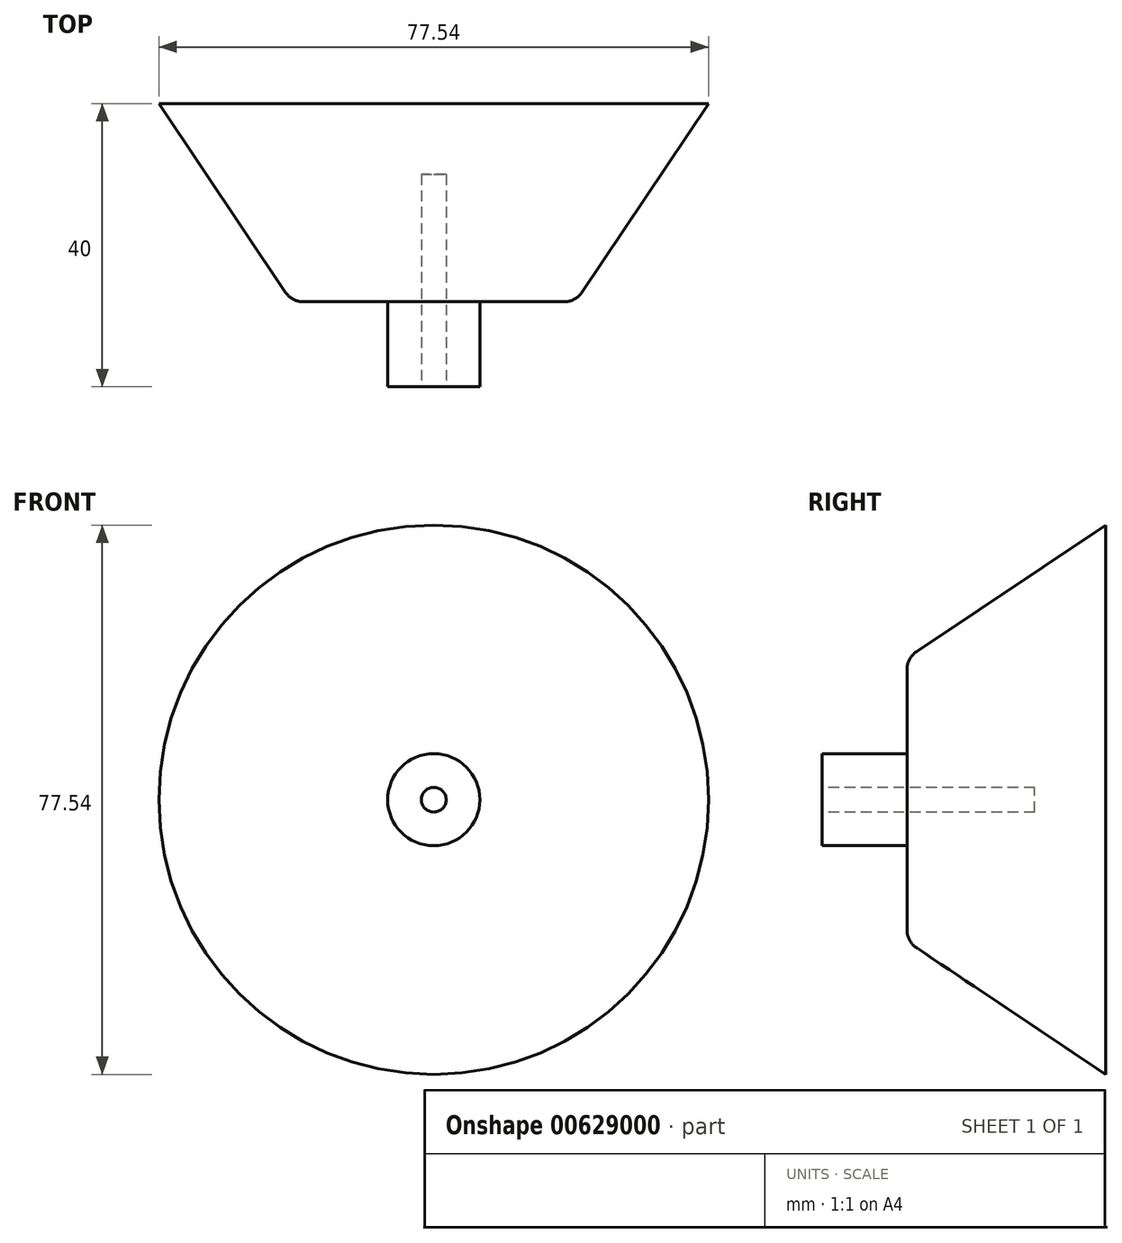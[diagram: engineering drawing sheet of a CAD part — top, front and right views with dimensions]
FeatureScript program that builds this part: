
annotation { "Feature Type Name" : "Feature", "Feature Type Description" : "" }
export const myFeature = defineFeature(function(context is Context, id is Id, definition is map)
    precondition{}
    {
        {
            var Q0;
            Q0=qCreatedBy(makeId("Front.planeOp"),FACE);
            var sketch = newSketch(context, id + "F0", { "sketchPlane" : qUnion([Q0])});
            skCircle(sketch, "E0", {"center": v(0, 0) * mm, "radius": 1.75 * mm});
            skCircle(sketch, "E1", {"center": v(0, 0) * mm, "radius": 6.5 * mm});
            skSolve(sketch);
        }
        {
            var Q0;
            Q0=qCreatedBy(makeId("Right.planeOp"),FACE);
            var sketch = newSketch(context, id + "F1", { "sketchPlane" : qUnion([Q0])});
            skLineSegment(sketch, "E2", {"start": v(0, 9.44) * mm, "end": v(0, -12.72) * mm, "construction": true});
            skLineSegment(sketch, "E3", {"start": v(12, 9.44) * mm, "end": v(12, -12.24) * mm, "construction": true});
            skLineSegment(sketch, "E4", {"start": v(40, 9.44) * mm, "end": v(40, -12.24) * mm, "construction": true});
            skLineSegment(sketch, "E5", {"start": v(12, 0) * mm, "end": v(12, 20) * mm});
            skLineSegment(sketch, "E6", {"start": v(40, 0) * mm, "end": v(12, 0) * mm});
            skLineSegment(sketch, "E7", {"start": v(5.3, 0) * mm, "end": v(66.6, 0) * mm, "construction": true});
            skLineSegment(sketch, "E8", {"start": v(12, 20) * mm, "end": v(40, 38.77) * mm});
            skLineSegment(sketch, "E9", {"start": v(40, 38.77) * mm, "end": v(40, 0) * mm});
            skSolve(sketch);
        }
        {
            var Q0;
            Q0=makeQuery(id+"F1.imprint","IMPRINT",FACE,{"disambiguationData":[TD([[makeQuery(id+"F1.imprint","IMPRINT",EDGE,{"derivedFrom":sQuery(id+"F1.wireOp",EDGE,"E5")}),-1.0]])]});
            var Q1;
            Q1=sQuery(id+"F1.wireOp",EDGE,"E7");
            revolve(context, id + "F2", {"entities" : qUnion([Q0]), "axis" : qUnion([Q1]), "revolveType" : RevolveType.FULL});
        }
        {
            var Q0;
            Q0=makeQuery(id+"F0.imprint","IMPRINT",FACE,{"disambiguationData":[TD([[makeQuery(id+"F0.imprint","IMPRINT",EDGE,{"derivedFrom":sQuery(id+"F0.wireOp",EDGE,"E0")}),-1.0]])]});
            extrude(context, id + "F3", {"entities" : qUnion([Q0]), "operationType" : NewBodyOperationType.ADD, "oppositeDirection" : true, "depth" : 20 * mm, "offsetDistance" : 25 * mm});
        }
        {
            var Q0;
            Q0=makeQuery(id+"F0.imprint","IMPRINT",FACE,{"disambiguationData":[TD([[makeQuery(id+"F0.imprint","IMPRINT",EDGE,{"derivedFrom":sQuery(id+"F0.wireOp",EDGE,"E0")}),1.0]])]});
            extrude(context, id + "F4", {"entities" : qUnion([Q0]), "operationType" : NewBodyOperationType.REMOVE, "oppositeDirection" : true, "depth" : 30 * mm, "offsetDistance" : 25 * mm});
        }
        {
            var Q0;
            Q0=makeQuery(id+"F2.opRevolve","SWEPT_EDGE",EDGE,{"disambiguationData":[OSD([sQuery(id+"F1.wireOp",EDGE,"E5"),sQuery(id+"F1.wireOp",EDGE,"E8")])]});
            fillet(context, id + "F5", {"entities" : qUnion([Q0]), "radius" : 3 * mm, "tangentPropagation" : true, "allowEdgeOverflow" : false});
        }
    });
